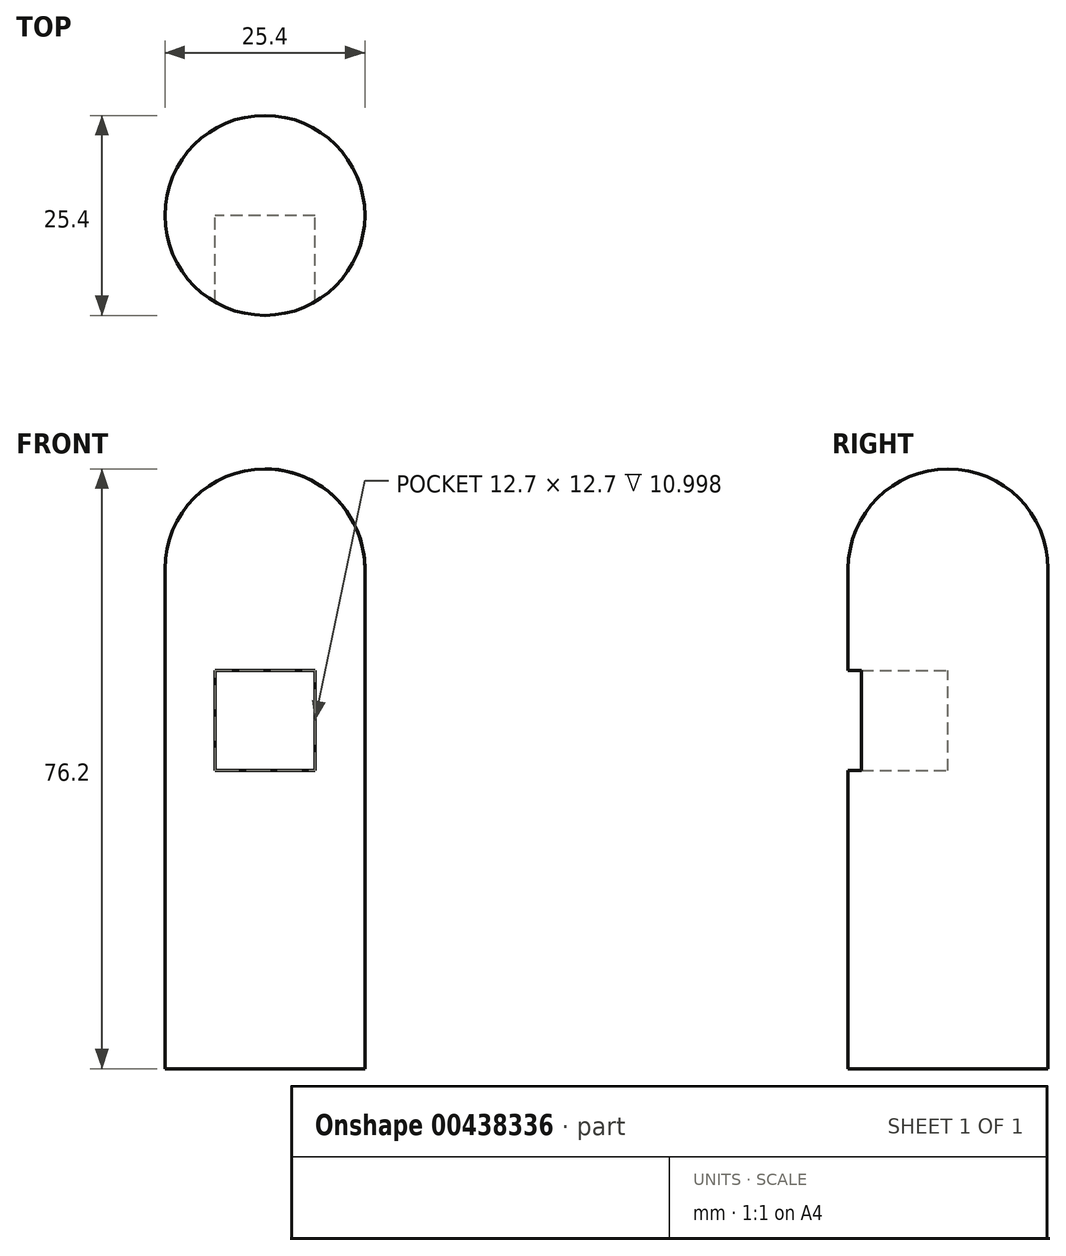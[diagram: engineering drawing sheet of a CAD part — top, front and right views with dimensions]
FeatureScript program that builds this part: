
annotation { "Feature Type Name" : "Feature", "Feature Type Description" : "" }
export const myFeature = defineFeature(function(context is Context, id is Id, definition is map)
    precondition{}
    {
        {
            var Q0;
            Q0=qCreatedBy(makeId("Top.planeOp"),FACE);
            var sketch = newSketch(context, id + "F0", { "sketchPlane" : qUnion([Q0])});
            skCircle(sketch, "E0", {"center": v(0, 0) * mm, "radius": 12.7 * mm});
            skSolve(sketch);
        }
        {
            var Q0;
            Q0 = qSketchRegion(id + "F0", true);
            extrude(context, id + "F1", {"entities" : qUnion([Q0]), "depth" : 76.2 * mm});
        }
        {
            var Q0;
            Q0=makeQuery(id+"F1.opExtrude","CAP_EDGE",EDGE,{"disambiguationData":[OSD([sQuery(id+"F0.wireOp",EDGE,"E0")])],"isStart":false});
            fillet(context, id + "F2", {"entities" : qUnion([Q0]), "radius" : 12.7 * mm, "tangentPropagation" : true, "allowEdgeOverflow" : false});
        }
        {
            var Q0;
            Q0=qCreatedBy(makeId("Front.planeOp"),FACE);
            var sketch = newSketch(context, id + "F3", { "sketchPlane" : qUnion([Q0])});
            skLineSegment(sketch, "E1", {"start": v(0, 0) * mm, "end": v(0, 37.87) * mm});
            skLineSegment(sketch, "E2", {"start": v(0, 37.87) * mm, "end": v(6.35, 37.87) * mm});
            skLineSegment(sketch, "E3.MirrorCS", {"start": v(0, 37.87) * mm, "end": v(-6.35, 37.87) * mm});
            skLineSegment(sketch, "E4", {"start": v(-6.35, 37.87) * mm, "end": v(-6.35, 50.57) * mm});
            skLineSegment(sketch, "E5.MirrorCS", {"start": v(6.35, 37.87) * mm, "end": v(6.35, 50.57) * mm});
            skLineSegment(sketch, "E6", {"start": v(-6.35, 50.57) * mm, "end": v(6.35, 50.57) * mm});
            skSolve(sketch);
        }
        {
            var Q0;
            Q0 = qSketchRegion(id + "F3", true);
            extrude(context, id + "F4", {"entities" : qUnion([Q0]), "operationType" : NewBodyOperationType.REMOVE, "depth" : 50.8 * mm});
        }
    });
